# Revit family: ASSA_ABLOY_MPD_RP300USD
name_source: partatom
category: Doors
units: mm (PartAtom-declared; Revit-internal decimal feet)

## family parameters
Always vertical = Yes
Cut with Voids When Loaded = No
Host = Wall
OmniClass Number = 23.30.10.00
OmniClass Title = Doors
Room Calculation Point = No
Shared = No

## types (1)
- ASSA_ABLOY_MPD_RP300USD
    Analytic Construction = <None>
    BottomProfileMaterial = Aluminum, Anodized Silver
    ClearanceZoneMaterial = ASSA ABLOY Clearance Zone
    Description = Machine Protection Door
    Function = Interior
    Height = 0 mm  [stored 0 ft]
    Manufacturer = ASSA ABLOY
    Model = RP300USD
    MotorCoverMaterial = Paint Finish RAL 9006
    TopRollMaterial = Aluminum, Anodized Silver
    URL = https://www.assaabloyentrance.com
    Wall Closure = By host
    Width = 0 mm  [stored 0 ft]

note: [stored X ft] marks values corroborated as IEEE doubles in the binary element streams (Revit-internal decimal feet)

## geometry (parser evidence)
native form markers: Sweep x31
no freeform markers — native parametric forms only
